# Revit family: QF_Dietatec_GENIER-475-FL
name_source: partatom
category: Specialty Equipment
revit_build: Autodesk Revit 2016 (Build: 20150220_1215(x64)
units: mm (PartAtom-declared; Revit-internal decimal feet)

## family parameters
Always vertical = Yes
Cut with Voids When Loaded = No
OmniClass Number = 23.40.40.14
OmniClass Title = Food Service Equipment
Part Type = Normal
Room Calculation Point = No
Round Connector Dimension = Use Diameter
Shared = No
Work Plane-Based = No

## types (4) — shared parameters
Accessory = No
Assembly Code = E1090320
Cold Water Flow = 0.0 L/s
Cold Water Size = 13 mm
Cold Water Temperature Recommended = 0 °C
Conn Conduit = No
Cycle = 50 Hz
Depth Actual = 1335 mm  [stored 4.37992 ft]
Height Actual = 1331 mm
Length Actual = 1630 mm
Manufacturer = DIETATEC
Max Overcurrent Protection = 0 A
Min Ckt Ampacity = 0 A
Number of Poles = 3
Phase = 3
URL = www.dietatec.com
Volts = 400 V
zero-valued in all types: Cost

## per-type parameters (varying)
| type | Apparent Power | Description | Electric power | FL Amps | Model | Weight |
| 58020 | 51000 VA | GENIER ACE MIXER KETTLE, 475L | 51000 W | 74 A | GENIER ACE 475 FL | 510.00 kg |
| 58039 | 51000 VA | GENIER GO MIXER KETTLE, 400L | 51000 W | 74 A | GENIER GO 400 FL | 485.00 kg |
| 58040 | 51000 VA | GENIER GO MIXER KETTLE, 475L | 51000 W | 74 A | GENIER GO 475 FL | 510.00 kg |
| 58060 | 49000 VA | GO-CLASSIC NON-MIXER KETTLE, 475L | 49000 W | 71 A | GO-CLASSIC 475 FL | 510.00 kg |

note: [stored X ft] marks values corroborated as IEEE doubles in the binary element streams (Revit-internal decimal feet)

## geometry (parser evidence)
native form markers: Sweep x5
no freeform markers — native parametric forms only
